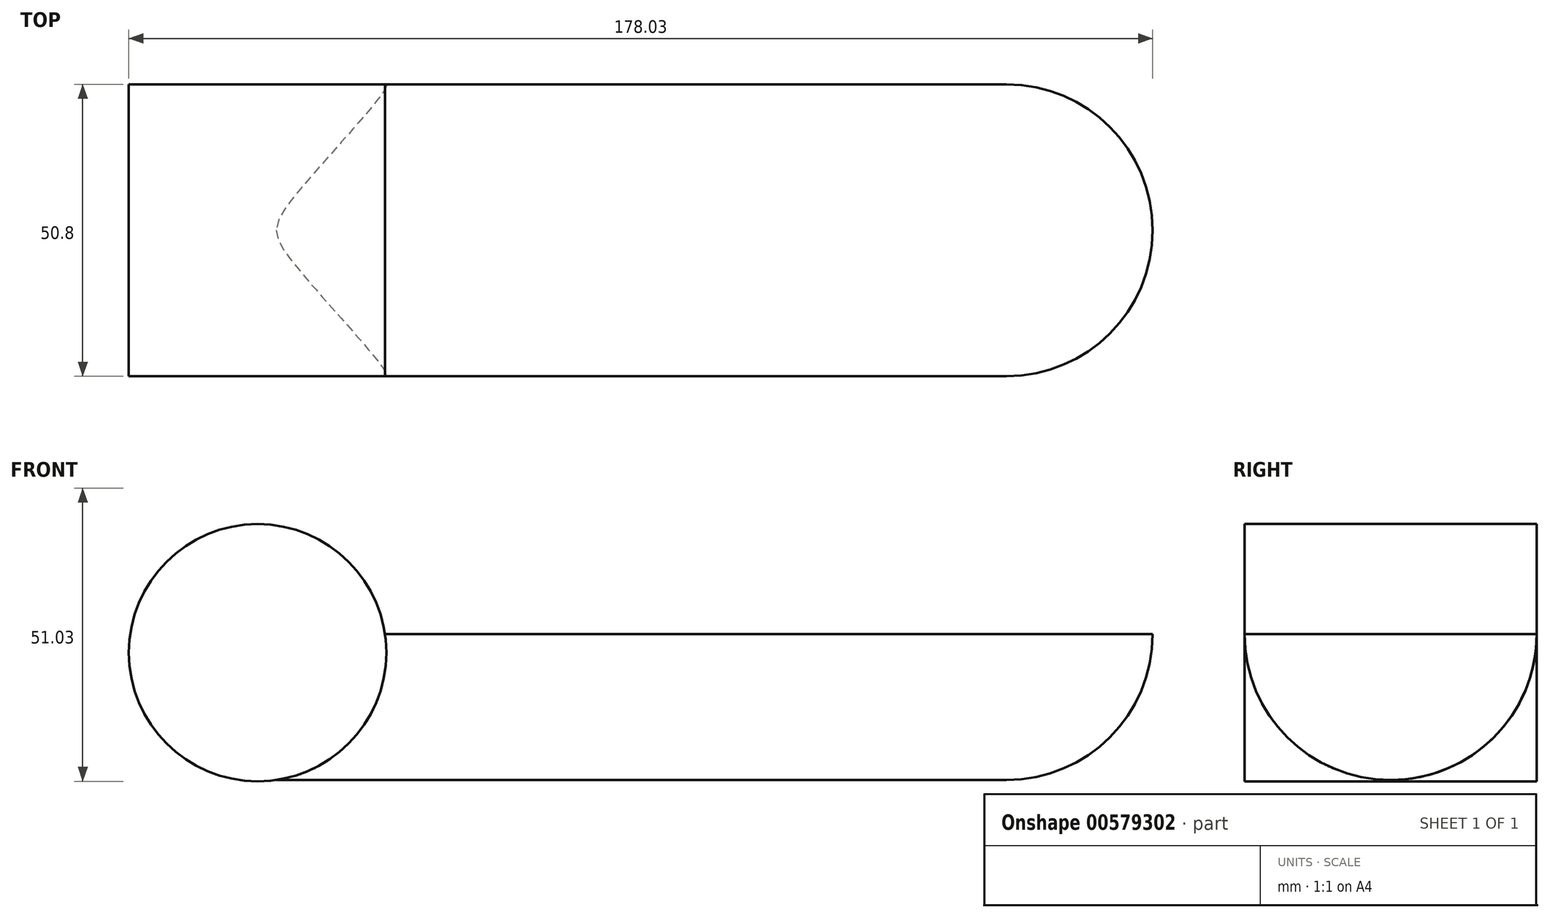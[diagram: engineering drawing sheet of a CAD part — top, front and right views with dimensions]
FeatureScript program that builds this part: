
annotation { "Feature Type Name" : "Feature", "Feature Type Description" : "" }
export const myFeature = defineFeature(function(context is Context, id is Id, definition is map)
    precondition{}
    {
        {
            var Q0;
            Q0=qCreatedBy(makeId("Front.planeOp"),FACE);
            var sketch = newSketch(context, id + "F0", { "sketchPlane" : qUnion([Q0])});
            skLineSegment(sketch, "E0.bottom", {"start": v(-72.57, -2.57) * mm, "end": v(54.43, -2.57) * mm});
            skLineSegment(sketch, "E0.top", {"start": v(-72.57, -27.97) * mm, "end": v(54.43, -27.97) * mm});
            skLineSegment(sketch, "E0.left", {"start": v(-72.57, -2.57) * mm, "end": v(-72.57, -27.97) * mm});
            skLineSegment(sketch, "E0.right", {"start": v(54.43, -2.57) * mm, "end": v(54.43, -27.97) * mm});
            skLineSegment(sketch, "E1", {"start": v(54.43, -2.57) * mm, "end": v(79.83, -2.57) * mm});
            skArc(sketch, "E2", {"start": v(54.43, -27.97) * mm, "mid": v(72.4, -20.53) * mm, "end": v(79.83, -2.57) * mm});
            skLineSegment(sketch, "E3", {"start": v(-72.57, -2.57) * mm, "end": v(-97.97, -2.57) * mm});
            skCircle(sketch, "E4", {"center": v(-75.81, -5.81) * mm, "radius": 22.39 * mm});
            skPoint(sketch, "E4.third.point", {"position": v(-86.7, -25.37) * mm});
            skSolve(sketch);
        }
        {
            var Q0;
            Q0 = qSketchRegion(id + "F0", true);
            extrude(context, id + "F1", {"entities" : qUnion([Q0]), "depth" : 50.8 * mm, "offsetDistance" : 25.4 * mm});
        }
        {
            var Q0;
            Q0=makeQuery(id+"F1.opExtrude","CAP_EDGE",EDGE,{"disambiguationData":[OSD([sQuery(id+"F0.wireOp",EDGE,"E0.top")])],"isStart":false});
            fillet(context, id + "F2", {"entities" : qUnion([Q0]), "radius" : 25.4 * mm, "tangentPropagation" : true, "allowEdgeOverflow" : false});
        }
        {
            var Q0;
            Q0=makeQuery(id+"F1.opExtrude","CAP_EDGE",EDGE,{"disambiguationData":[OSD([sQuery(id+"F0.wireOp",EDGE,"E0.top")])],"isStart":true});
            fillet(context, id + "F3", {"entities" : qUnion([Q0]), "radius" : 25.4 * mm, "tangentPropagation" : true, "allowEdgeOverflow" : false});
        }
    });
